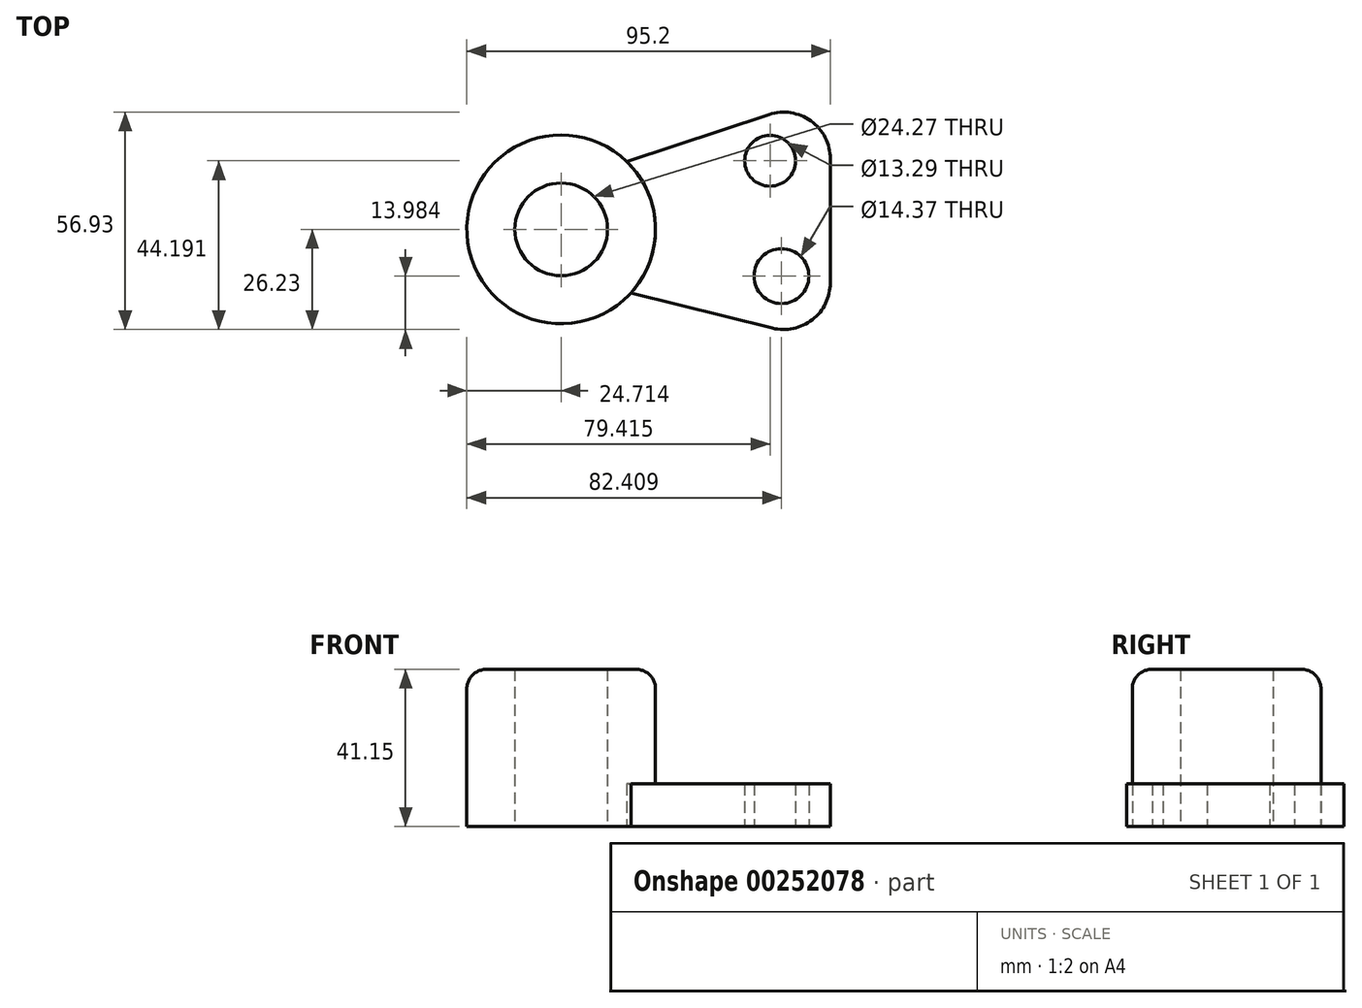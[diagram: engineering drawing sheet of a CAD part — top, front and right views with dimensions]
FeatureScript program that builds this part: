
annotation { "Feature Type Name" : "Feature", "Feature Type Description" : "" }
export const myFeature = defineFeature(function(context is Context, id is Id, definition is map)
    precondition{}
    {
        {
            var Q0;
            Q0=qCreatedBy(makeId("Top.planeOp"),FACE);
            var sketch = newSketch(context, id + "F0", { "sketchPlane" : qUnion([Q0])});
            skCircle(sketch, "E0", {"center": v(-45.18, 0) * mm, "radius": 24.71 * mm});
            skLineSegment(sketch, "E1", {"start": v(-28.01, 17.78) * mm, "end": v(25.3, 35.38) * mm});
            skLineSegment(sketch, "E2", {"start": v(25.3, 35.38) * mm, "end": v(25.3, -29.66) * mm});
            skLineSegment(sketch, "E3", {"start": v(25.3, -29.66) * mm, "end": v(-26.89, -16.62) * mm});
            skCircle(sketch, "E4", {"center": v(-45.18, 0) * mm, "radius": 12.14 * mm});
            skCircle(sketch, "E5", {"center": v(9.53, 17.96) * mm, "radius": 6.64 * mm});
            skCircle(sketch, "E6", {"center": v(12.52, -12.25) * mm, "radius": 7.18 * mm});
            skSolve(sketch);
        }
        {
            var Q0;
            Q0=makeQuery(id+"F0.imprint","IMPRINT",FACE,{"disambiguationData":[TD([[makeQuery(id+"F0.imprint","IMPRINT",EDGE,{"derivedFrom":sQuery(id+"F0.wireOp",EDGE,"E4")}),-1.0]])]});
            extrude(context, id + "F1", {"entities" : qUnion([Q0]), "depth" : 41.15 * mm});
        }
        {
            var Q0;
            Q0=makeQuery(id+"F1.opExtrude","CAP_EDGE",EDGE,{"disambiguationData":[OSD([sQuery(id+"F0.wireOp",EDGE,"E0")])],"isStart":false});
            fillet(context, id + "F2", {"entities" : qUnion([Q0]), "radius" : 5.08 * mm, "tangentPropagation" : true, "allowEdgeOverflow" : false});
        }
        {
            var Q0;
            {var subQ0=sQuery(id+"F0.wireOp",EDGE,"E1");Q0=makeQuery(id+"F0.imprint","IMPRINT",FACE,{"disambiguationData":[TD([[makeQuery(id+"F0.imprint","IMPRINT",EDGE,{"derivedFrom":subQ0}),-1.0]])]});}
            extrude(context, id + "F3", {"entities" : qUnion([Q0]), "operationType" : NewBodyOperationType.ADD, "depth" : 11.18 * mm});
        }
        {
            var Q0;
            Q0=makeQuery(id+"F3.opExtrude","SWEPT_EDGE",EDGE,{"disambiguationData":[OSD([sQuery(id+"F0.wireOp",EDGE,"E2"),sQuery(id+"F0.wireOp",EDGE,"E3")])]});
            var Q1;
            Q1=makeQuery(id+"F3.opExtrude","SWEPT_EDGE",EDGE,{"disambiguationData":[OSD([sQuery(id+"F0.wireOp",EDGE,"E1"),sQuery(id+"F0.wireOp",EDGE,"E2")])]});
            fillet(context, id + "F4", {"entities" : qUnion([Q0, Q1]), "radius" : 12.22 * mm, "tangentPropagation" : true, "allowEdgeOverflow" : false});
        }
        {
            var Q0;
            Q0=qCreatedBy(makeId("Top.planeOp"),FACE);
            cPlane(context, id + "F5", {"entities" : qUnion([Q0]), "cplaneType" : CPlaneType.OFFSET, "offset" : 35.81 * mm, "width" : 152.4 * mm, "height" : 152.4 * mm});
        }
    });
